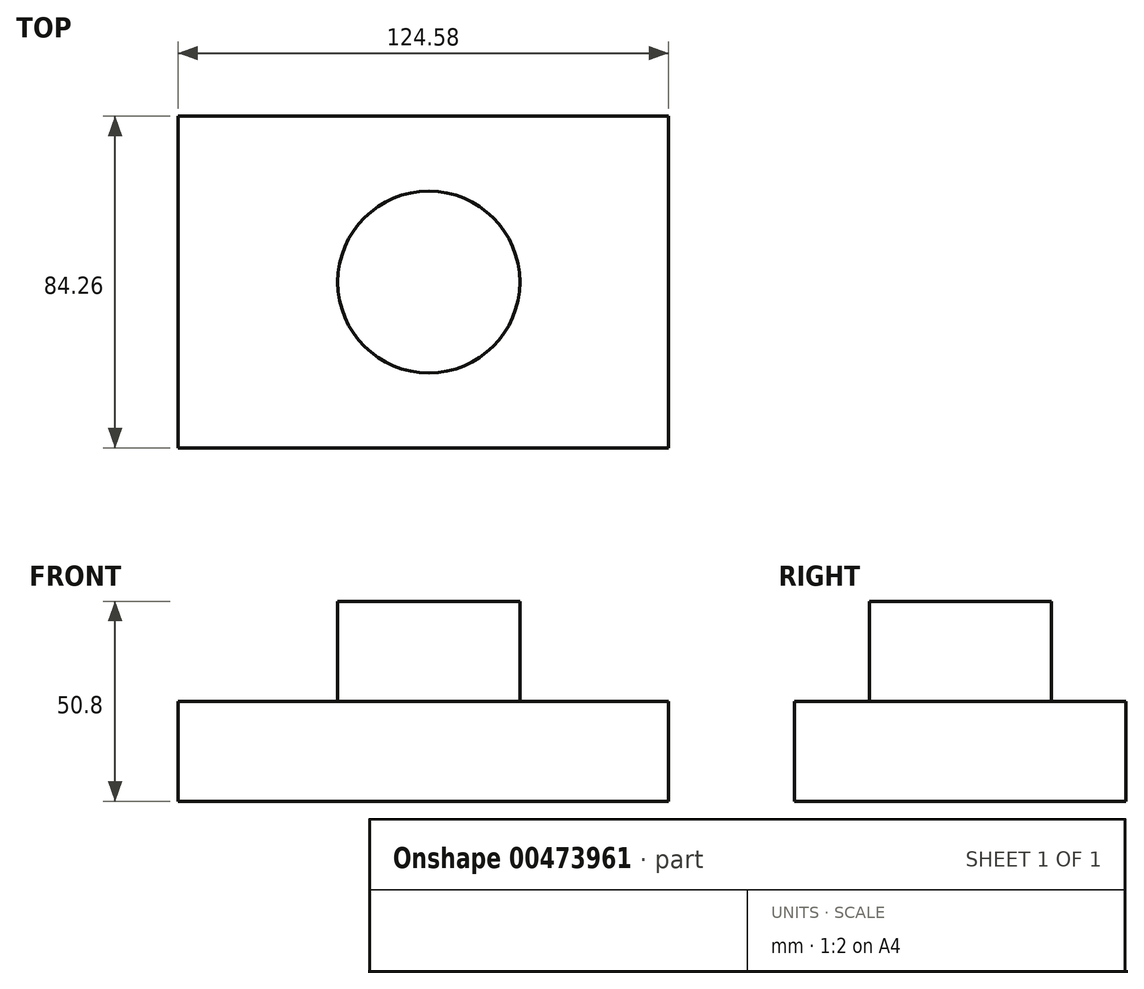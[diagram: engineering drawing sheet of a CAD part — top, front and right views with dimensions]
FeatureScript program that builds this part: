
annotation { "Feature Type Name" : "Feature", "Feature Type Description" : "" }
export const myFeature = defineFeature(function(context is Context, id is Id, definition is map)
    precondition{}
    {
        {
            var Q0;
            Q0=qCreatedBy(makeId("Top.planeOp"),FACE);
            var sketch = newSketch(context, id + "F0", { "sketchPlane" : qUnion([Q0])});
            skLineSegment(sketch, "E0.bottom", {"start": v(62.3, -42.13) * mm, "end": v(-62.3, -42.13) * mm});
            skLineSegment(sketch, "E0.top", {"start": v(62.3, 42.13) * mm, "end": v(-62.3, 42.13) * mm});
            skLineSegment(sketch, "E0.left", {"start": v(62.3, -42.13) * mm, "end": v(62.3, 42.13) * mm});
            skLineSegment(sketch, "E0.right", {"start": v(-62.3, -42.13) * mm, "end": v(-62.3, 42.13) * mm});
            skPoint(sketch, "E0.middle", {"position": v(0, 0) * mm});
            skSolve(sketch);
        }
        {
            var Q0;
            Q0=makeQuery(id+"F0.imprint","IMPRINT",FACE,{"disambiguationData":[TD([[makeQuery(id+"F0.imprint","IMPRINT",EDGE,{"derivedFrom":sQuery(id+"F0.wireOp",EDGE,"E0.bottom")}),-1.0]])]});
            extrude(context, id + "F1", {"entities" : qUnion([Q0]), "depth" : 25.4 * mm, "offsetDistance" : 25.4 * mm});
        }
        {
            var Q0;
            Q0=makeQuery(id+"F1.opExtrude","CAP_FACE",FACE,{"disambiguationData":[OSD([sQuery(id+"F0.wireOp",EDGE,"E0.bottom"),sQuery(id+"F0.wireOp",EDGE,"E0.top"),sQuery(id+"F0.wireOp",EDGE,"E0.left"),sQuery(id+"F0.wireOp",EDGE,"E0.right")])],"isStart":false});
            var sketch = newSketch(context, id + "F2", { "sketchPlane" : qUnion([Q0])});
            skCircle(sketch, "E1", {"center": v(1.4, 0) * mm, "radius": 23.12 * mm});
            skSolve(sketch);
        }
        {
            var Q0;
            Q0 = qSketchRegion(id + "F2", true);
            extrude(context, id + "F3", {"entities" : qUnion([Q0]), "operationType" : NewBodyOperationType.ADD, "depth" : 25.4 * mm, "offsetDistance" : 25.4 * mm});
        }
    });
